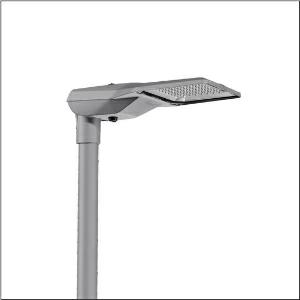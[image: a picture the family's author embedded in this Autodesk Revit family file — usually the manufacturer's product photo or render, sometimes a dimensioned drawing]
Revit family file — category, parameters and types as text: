
# Revit family: streetlight_sl_21_iq_midi___pl52_5xe3h31y08mb_cc6d
name_source: partatom
category: Lighting Fixtures
units: mm (PartAtom-declared; Revit-internal decimal feet)

## family parameters
Cut with Voids When Loaded = No
Host = Face
Light Source = No
Part Type = Normal
Room Calculation Point = No
Round Connector Dimension = Use Diameter
Shared = No

## types (1)
- --- (1 x LED, 18020 lm, 129.3 W, 3000K)
    Apparent Load = 129 VA
    CIE Flux Codes = 27 59 98 100 100
    Color Rendering = 70
    Color Temperature = 3000K
    Default Elevation = 1800 mm
    Description = Streetlight SL 21 iQ midi, mast luminaire, primary light control with lens, of PMMA, primary optical cover: cover, of toughened safety glass, transparent, light distribution: PL52, light emission: direct distribution, primary light characteristic: asymmetric, installation type: post-top, side-entry, LED, High Power LED, rated luminous flux: 18.020lm, luminous efficacy: 139lm/W, light colour: 730, colour temperature: 3000K, control: presetting dimming logarithmic, Street-Remote, Auto-Match, Temp-Guard, Lumen-Switch, Night-Set, Smart-Wire, Light-Fading, Desk-Remote (wireless, voltage-free reading and setting of iQ features in the workshop via application-optimized NFC function/RFID function), optimised constant luminous flux control (CLO 2.0), mains connection: 230..240V, AC, 50/60Hz, start of lifetime: 129W, end of service life: 142W, reduction: 56W, luminaire housing, of diecast aluminium, powder-coated, Siteco® metallic grey (DB 702S), corrosivity category C5 mid according to DIN EN ISO 12944, please order mast flange separately, inclination adjustable: 0°, 5°, 10°, 15°, sealing non-destructively replaceable, multi-level sealing system, length: 644mm, width: 335mm, height: 110mm, mast flange for spigot size: 42mm (side-entry): 5XC10008XM4, 60/48mm (side-entry/post-top): 5XC10108XM2, 76/60mm (side-entry/post-top): 5XC10108XM1, Smart Interface below and above, protection rating (complete): IP66, insulation class (complete): insulation class II (safety insulation), certification: CE, ENEC, ENEC+, VDE, impact resistance: IK09, permissible operating ambient temperature for outdoor applications: -40..+50°C, standard-compliant lighting for roads and squares, packaging unit: 1 piece

Light Distribution: PL52
    Height = 111 mm
    Lamp = 1 x LED
    Lamp Light Flux = 18020 lm
    Lamp Power = 129.3 W
    Lamp count = 1
    Length = 644 mm
    Luminous efficacy = 139 lm/W
    Manufacturer = Siteco
    ModVariant = No
    Model = 5XE3H31Y08MB
    Number of Poles = 1
    OnlyDefault = Yes
    Power Factor = 1
    Product Name = Streetlight SL 21 iQ midi | PL52
    Product group = mast luminaire | pylon top
    ProductGroupID = 6100
    Protection Class = Protection class II
    Protection Degree = IP 66
    RLX_Detail_Level = 1
    RLX_Emergency_Light_Flux = 0 lm
    RLX_Emergency_Type = 0
    RLX_Emergency_Type_DB = No
    RlxData = <blob elided: 100777 chars, md5=9b85c8ae>
    Socket = socket
    Standby Power = 0 W
    System Light Flux = 18021 lm
    System Power = 129 W
    Type Comments = factory setting: luminous flux: 100 % | dim-lin: 254 | 672 mA
    Type Image = l_1004304.jpg
    URL = http://relux.com
    VarID = @adj_045913
    Voltage = 0 V
    Weight = 0.00 kg
    Width = 336 mm

## geometry (parser evidence)
native form markers: Blend x4, Sweep x12
no freeform markers — native parametric forms only
